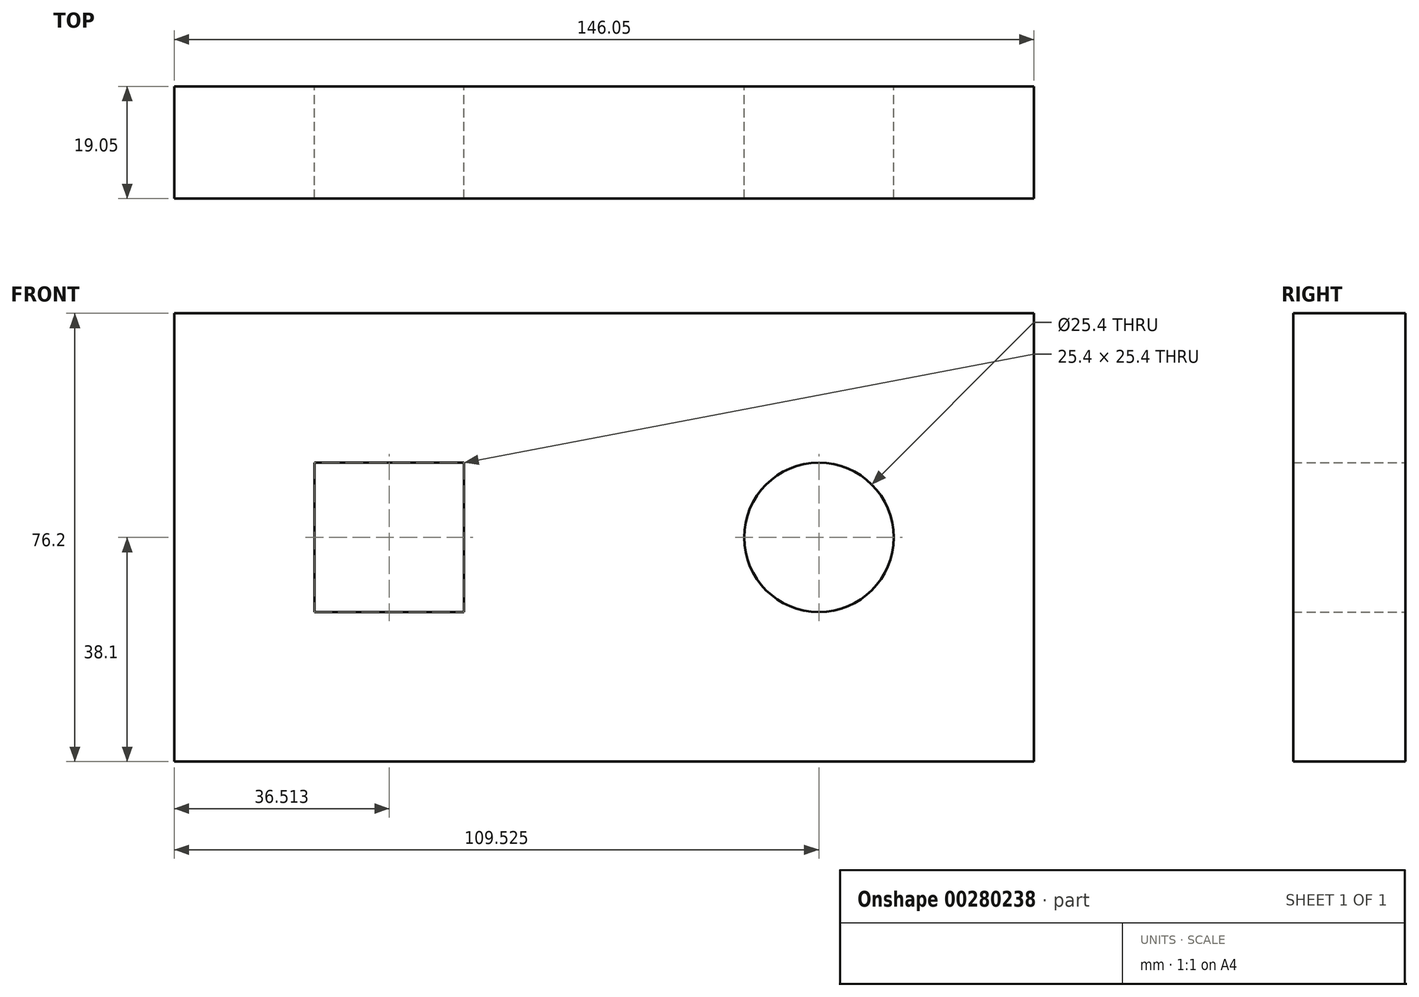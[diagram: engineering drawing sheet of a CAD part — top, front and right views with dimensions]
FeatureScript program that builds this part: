
annotation { "Feature Type Name" : "Feature", "Feature Type Description" : "" }
export const myFeature = defineFeature(function(context is Context, id is Id, definition is map)
    precondition{}
    {
        {
            var Q0;
            Q0=qCreatedBy(makeId("Front.planeOp"),FACE);
            var sketch = newSketch(context, id + "F0", { "sketchPlane" : qUnion([Q0])});
            skLineSegment(sketch, "E0.bottom", {"start": v(0, 0) * mm, "end": v(-146.05, 0) * mm});
            skLineSegment(sketch, "E0.top", {"start": v(0, 76.2) * mm, "end": v(-146.05, 76.2) * mm});
            skLineSegment(sketch, "E0.left", {"start": v(0, 0) * mm, "end": v(0, 76.2) * mm});
            skLineSegment(sketch, "E0.right", {"start": v(-146.05, 0) * mm, "end": v(-146.05, 76.2) * mm});
            skCircle(sketch, "E1", {"center": v(-36.53, 38.1) * mm, "radius": 12.7 * mm});
            skLineSegment(sketch, "E2.bottom", {"start": v(-122.24, 50.8) * mm, "end": v(-96.84, 50.8) * mm});
            skLineSegment(sketch, "E2.top", {"start": v(-122.24, 25.4) * mm, "end": v(-96.84, 25.4) * mm});
            skLineSegment(sketch, "E2.left", {"start": v(-122.24, 50.8) * mm, "end": v(-122.24, 25.4) * mm});
            skLineSegment(sketch, "E2.right", {"start": v(-96.84, 50.8) * mm, "end": v(-96.84, 25.4) * mm});
            skSolve(sketch);
        }
        {
            var Q0;
            Q0=makeQuery(id+"F0.imprint","IMPRINT",FACE,{"disambiguationData":[TD([[makeQuery(id+"F0.imprint","IMPRINT",EDGE,{"derivedFrom":sQuery(id+"F0.wireOp",EDGE,"E0.bottom")}),-1.0]])]});
            extrude(context, id + "F1", {"entities" : qUnion([Q0]), "depth" : 19.05 * mm});
        }
    });
